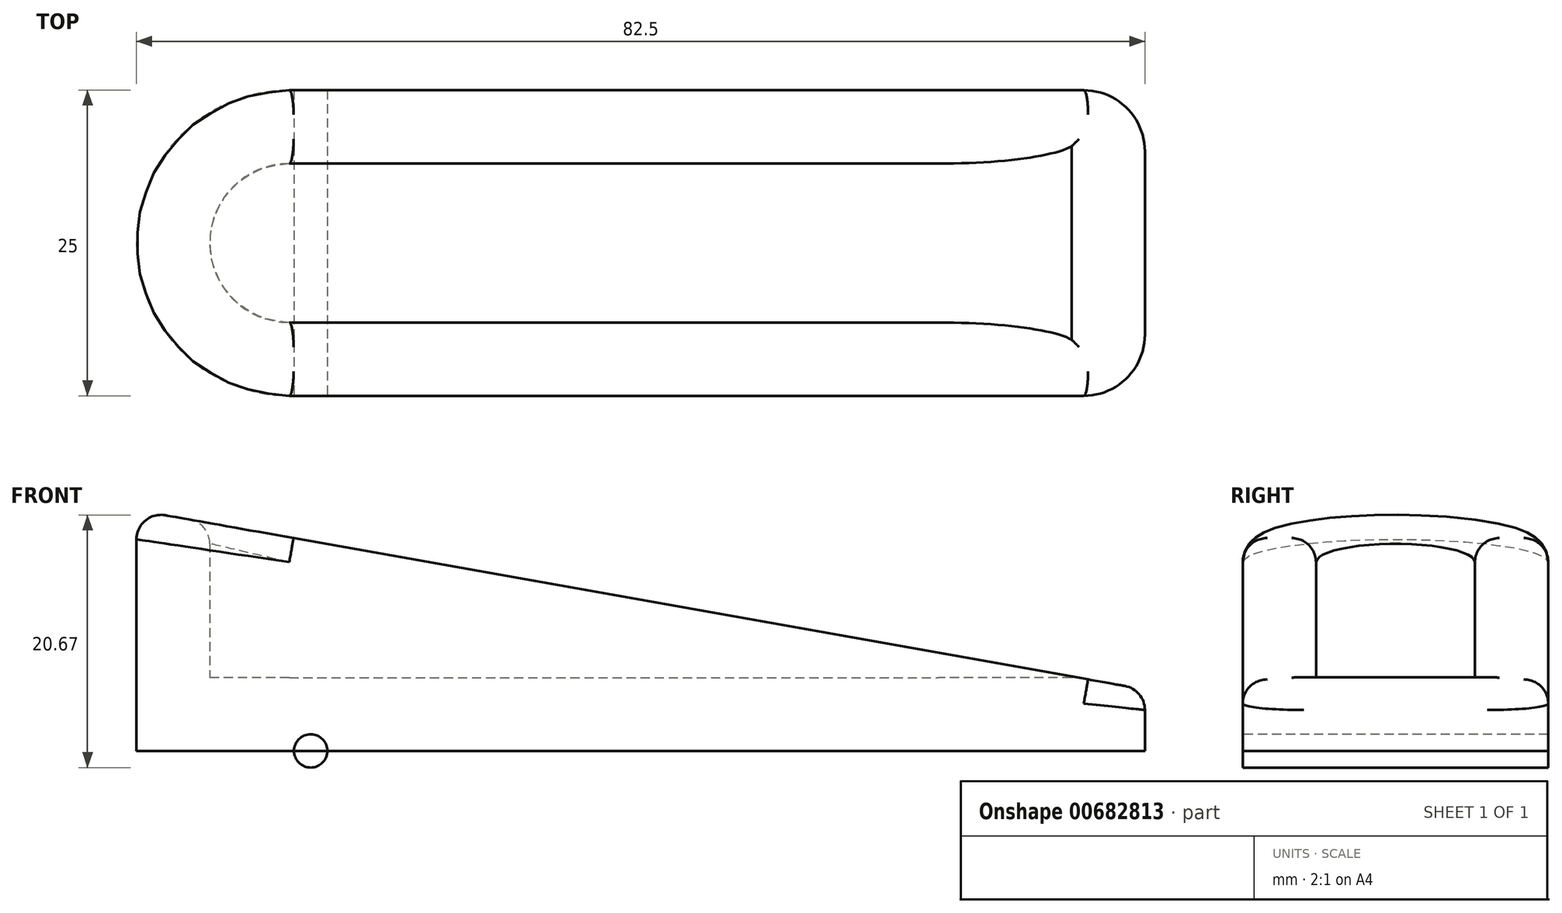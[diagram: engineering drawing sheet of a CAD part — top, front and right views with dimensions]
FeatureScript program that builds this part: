
annotation { "Feature Type Name" : "Feature", "Feature Type Description" : "" }
export const myFeature = defineFeature(function(context is Context, id is Id, definition is map)
    precondition{}
    {
        {
            var Q0;
            Q0=qCreatedBy(makeId("Top.planeOp"),FACE);
            var sketch = newSketch(context, id + "F0", { "sketchPlane" : qUnion([Q0])});
            skLineSegment(sketch, "E0.bottom", {"start": v(-33.67, 15.66) * mm, "end": v(31.33, 15.66) * mm});
            skLineSegment(sketch, "E0.top", {"start": v(-33.67, -9.34) * mm, "end": v(31.33, -9.34) * mm});
            skLineSegment(sketch, "E0.right", {"start": v(36.33, 10.66) * mm, "end": v(36.33, -4.34) * mm});
            skArc(sketch, "E1", {"start": v(-33.67, 15.66) * mm, "mid": v(-46.17, 3.16) * mm, "end": v(-33.67, -9.34) * mm});
            skPoint(sketch, "E2.visualSharp", {"position": v(36.33, 15.66) * mm});
            skArc(sketch, "E2.filletArc", {"start": v(36.33, 10.66) * mm, "mid": v(34.86, 14.2) * mm, "end": v(31.33, 15.66) * mm});
            skPoint(sketch, "E3.visualSharp", {"position": v(36.33, -9.34) * mm});
            skArc(sketch, "E3.filletArc", {"start": v(31.33, -9.34) * mm, "mid": v(34.86, -7.88) * mm, "end": v(36.33, -4.34) * mm});
            skSolve(sketch);
        }
        {
            var Q0;
            Q0 = qSketchRegion(id + "F0", true);
            extrude(context, id + "F1", {"entities" : qUnion([Q0]), "depth" : 25 * mm, "offsetDistance" : 25 * mm});
        }
        {
            var Q0;
            Q0=makeQuery(id+"F1.opExtrude","CAP_FACE",FACE,{"disambiguationData":[OSD([sQuery(id+"F0.wireOp",EDGE,"E0.bottom"),sQuery(id+"F0.wireOp",EDGE,"E0.top"),sQuery(id+"F0.wireOp",EDGE,"E0.right"),sQuery(id+"F0.wireOp",EDGE,"E1"),sQuery(id+"F0.wireOp",EDGE,"E2.filletArc"),sQuery(id+"F0.wireOp",EDGE,"E3.filletArc")])],"isStart":false});
            shell(context, id + "F2", {"entities" : qUnion([Q0]), "thickness" : 6 * mm});
        }
        {
            var Q0;
            Q0=makeQuery(id+"F1.opExtrude","CAP_FACE",FACE,{"disambiguationData":[OSD([sQuery(id+"F0.wireOp",EDGE,"E0.bottom"),sQuery(id+"F0.wireOp",EDGE,"E0.top"),sQuery(id+"F0.wireOp",EDGE,"E0.right"),sQuery(id+"F0.wireOp",EDGE,"E1"),sQuery(id+"F0.wireOp",EDGE,"E2.filletArc"),sQuery(id+"F0.wireOp",EDGE,"E3.filletArc")])],"isStart":false});
            fillet(context, id + "F3", {"entities" : qUnion([Q0]), "radius" : 2 * mm, "tangentPropagation" : true, "allowEdgeOverflow" : false});
        }
        {
            var Q0;
            Q0=qCreatedBy(makeId("Front.planeOp"),FACE);
            var sketch = newSketch(context, id + "F4", { "sketchPlane" : qUnion([Q0])});
            skLineSegment(sketch, "E4", {"start": v(-51.71, 20.69) * mm, "end": v(42.67, 3.9) * mm});
            skLineSegment(sketch, "E5", {"start": v(42.67, 3.9) * mm, "end": v(42.67, 33.3) * mm});
            skLineSegment(sketch, "E6", {"start": v(42.67, 33.3) * mm, "end": v(-49.28, 33.3) * mm});
            skLineSegment(sketch, "E7", {"start": v(-49.28, 33.3) * mm, "end": v(-51.71, 20.69) * mm});
            skSolve(sketch);
        }
        {
            var Q0;
            Q0=makeQuery(id+"F4.imprint","IMPRINT",FACE,{"disambiguationData":[TD([[makeQuery(id+"F4.imprint","IMPRINT",EDGE,{"derivedFrom":sQuery(id+"F4.wireOp",EDGE,"E4")}),1.0]])]});
            extrude(context, id + "F5", {"entities" : qUnion([Q0]), "operationType" : NewBodyOperationType.REMOVE, "endBound" : BoundingType.SYMMETRIC, "depth" : 40 * mm, "offsetDistance" : 25 * mm});
        }
        {
            var Q0;
            Q0=makeQuery(id+"F5.boolean.opBoolean","COPY",FACE,{"derivedFrom":makeQuery(id+"F5.opExtrude","SWEPT_FACE",FACE,{"disambiguationData":[OSD([sQuery(id+"F4.wireOp",EDGE,"E4")])]})});
            fillet(context, id + "F6", {"entities" : qUnion([Q0]), "radius" : 2 * mm, "tangentPropagation" : true, "allowEdgeOverflow" : false});
        }
        {
            var Q0;
            Q0=makeQuery(id+"F1.opExtrude","SWEPT_FACE",FACE,{"disambiguationData":[OSD([sQuery(id+"F0.wireOp",EDGE,"E0.top")])]});
            var sketch = newSketch(context, id + "F7", { "sketchPlane" : qUnion([Q0])});
            skCircle(sketch, "E8", {"center": v(-31.92, 0) * mm, "radius": 1.36 * mm});
            skSolve(sketch);
        }
        {
            var Q0;
            {var subQ0=sQuery(id+"F7.wireOp",EDGE,"E8");var subQ1=makeQuery(id+"F1.opExtrude","CAP_EDGE",EDGE,{"disambiguationData":[OSD([sQuery(id+"F0.wireOp",EDGE,"E0.top")])],"isStart":true});var subQ2=makeQuery(id+"F7.imprint","INTERSECT",VERTEX,{"disambiguationData":[OD(0.0)],"derivedFrom":[subQ1,subQ0]});Q0=makeQuery(id+"F7.imprint","IMPRINT",FACE,{"disambiguationData":[TD([[makeQuery(id+"F7.imprint","IMPRINT",EDGE,{"disambiguationData":[TD([[subQ2,-1.0]])],"derivedFrom":subQ0}),1.0]])]});}
            var Q1;
            {var subQ0=sQuery(id+"F7.wireOp",EDGE,"E8");var subQ1=makeQuery(id+"F1.opExtrude","CAP_EDGE",EDGE,{"disambiguationData":[OSD([sQuery(id+"F0.wireOp",EDGE,"E0.top")])],"isStart":true});var subQ2=makeQuery(id+"F7.imprint","INTERSECT",VERTEX,{"disambiguationData":[OD(0.0)],"derivedFrom":[subQ1,subQ0]});Q1=makeQuery(id+"F7.imprint","IMPRINT",FACE,{"disambiguationData":[TD([[makeQuery(id+"F7.imprint","IMPRINT",EDGE,{"disambiguationData":[TD([[subQ2,1.0]])],"derivedFrom":subQ0}),1.0]])]});}
            var Q2;
            Q2=sQuery(id+"F7.wireOp",EDGE,"E8");
            extrude(context, id + "F8", {"entities" : qUnion([Q0, Q1]), "surfaceEntities" : qUnion([Q2]), "oppositeDirection" : true, "depth" : 25 * mm, "offsetDistance" : 25 * mm});
        }
    });
